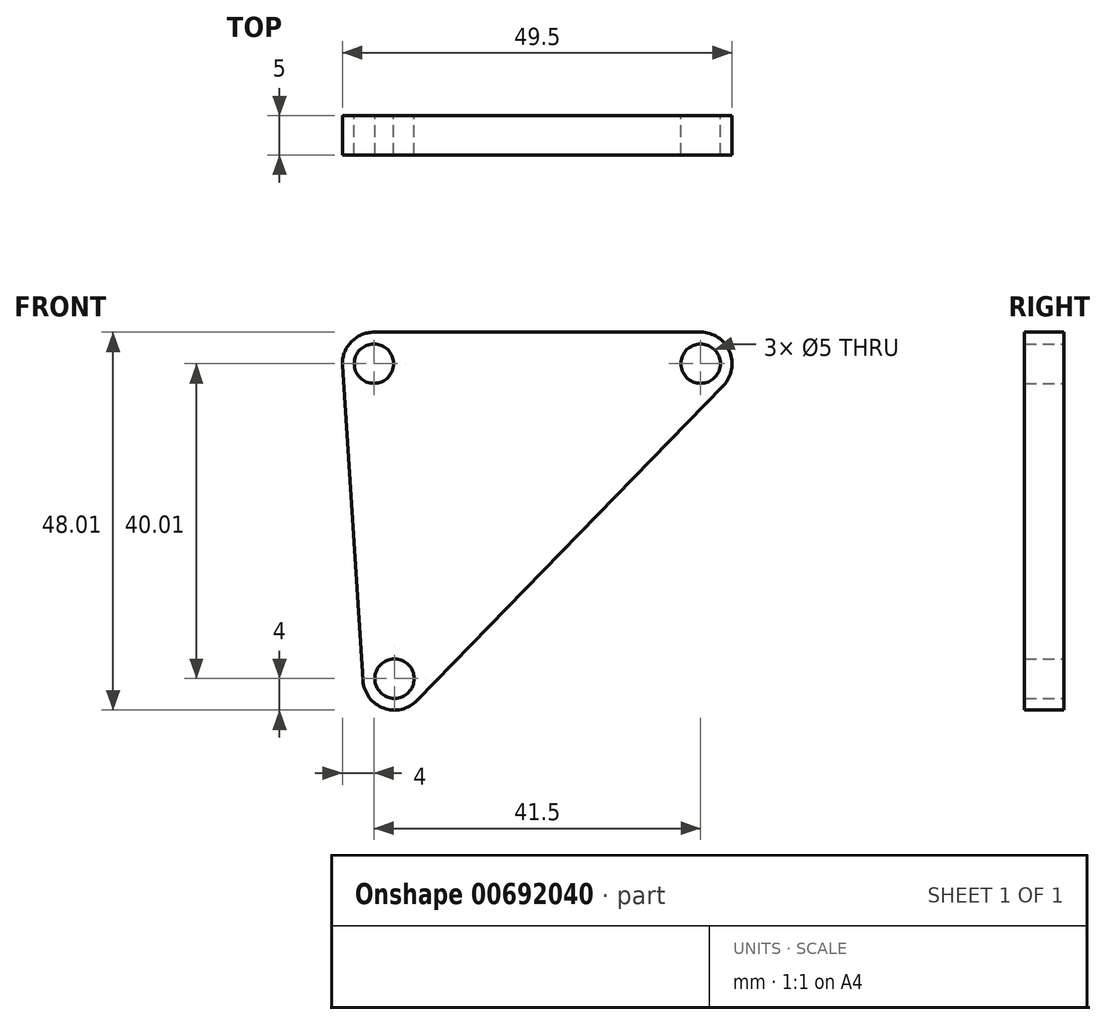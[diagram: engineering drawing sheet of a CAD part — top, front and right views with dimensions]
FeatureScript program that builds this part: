
annotation { "Feature Type Name" : "Feature", "Feature Type Description" : "" }
export const myFeature = defineFeature(function(context is Context, id is Id, definition is map)
    precondition{}
    {
        {
            var Q0;
            Q0=qCreatedBy(makeId("Front.planeOp"),FACE);
            var sketch = newSketch(context, id + "F0", { "sketchPlane" : qUnion([Q0])});
            skArc(sketch, "E0", {"start": v(-15.71, 6.74) * mm, "mid": v(-18.63, 5.47) * mm, "end": v(-19.7, 2.48) * mm});
            skArc(sketch, "E1", {"start": v(28.66, -0.05) * mm, "mid": v(29.47, 4.3) * mm, "end": v(25.79, 6.74) * mm});
            skArc(sketch, "E2", {"start": v(-17.1, -37.53) * mm, "mid": v(-14.48, -41.02) * mm, "end": v(-10.23, -40.06) * mm});
            skLineSegment(sketch, "E3", {"start": v(-19.7, 2.48) * mm, "end": v(-17.1, -37.53) * mm});
            skLineSegment(sketch, "E4", {"start": v(-10.23, -40.06) * mm, "end": v(28.66, -0.05) * mm});
            skLineSegment(sketch, "E5", {"start": v(-15.71, 6.74) * mm, "end": v(25.79, 6.74) * mm});
            skCircle(sketch, "E6", {"center": v(-15.71, 2.74) * mm, "radius": 2.5 * mm});
            skCircle(sketch, "E7", {"center": v(25.79, 2.74) * mm, "radius": 2.5 * mm});
            skCircle(sketch, "E8", {"center": v(-13.1, -37.27) * mm, "radius": 2.5 * mm});
            skSolve(sketch);
        }
        {
            var Q0;
            Q0=makeQuery(id+"F0.imprint","IMPRINT",FACE,{"disambiguationData":[TD([[makeQuery(id+"F0.imprint","IMPRINT",EDGE,{"derivedFrom":sQuery(id+"F0.wireOp",EDGE,"E0")}),1.0]])]});
            extrude(context, id + "F1", {"entities" : qUnion([Q0]), "depth" : 5 * mm, "offsetDistance" : 25 * mm});
        }
    });
